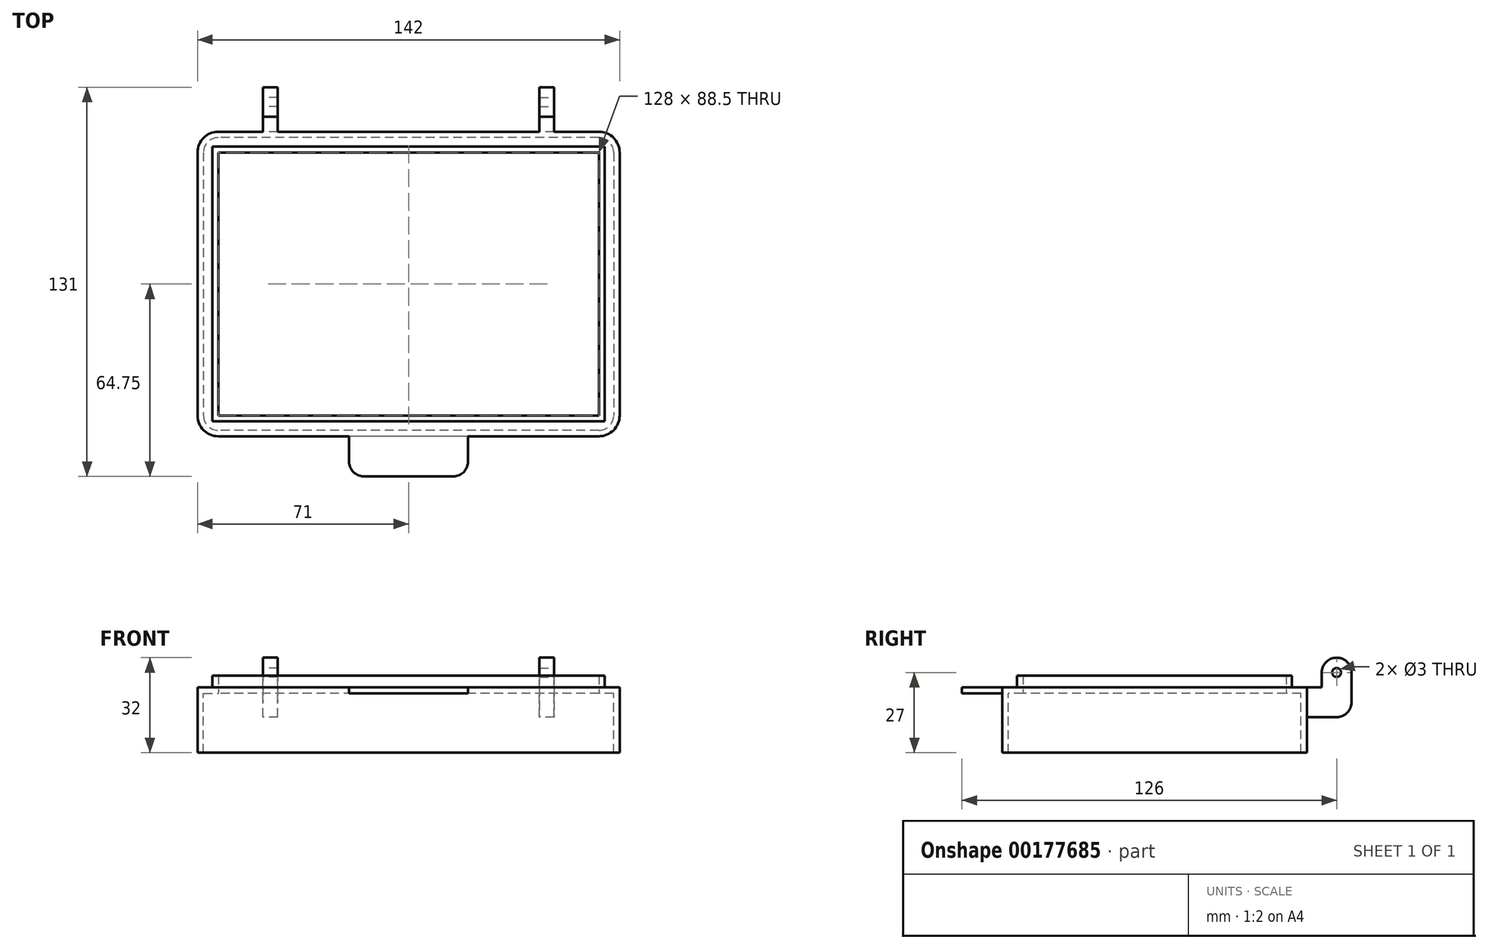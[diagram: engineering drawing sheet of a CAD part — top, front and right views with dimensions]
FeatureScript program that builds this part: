
annotation { "Feature Type Name" : "Feature", "Feature Type Description" : "" }
export const myFeature = defineFeature(function(context is Context, id is Id, definition is map)
    precondition{}
    {
        {
            var Q0;
            Q0=qCreatedBy(makeId("Top.planeOp"),FACE);
            var sketch = newSketch(context, id + "F0", { "sketchPlane" : qUnion([Q0])});
            skLineSegment(sketch, "E0.bottom", {"start": v(64, 49.25) * mm, "end": v(-64, 49.25) * mm});
            skLineSegment(sketch, "E0.top", {"start": v(64, -49.25) * mm, "end": v(-64, -49.25) * mm});
            skLineSegment(sketch, "E0.left", {"start": v(69, 44.25) * mm, "end": v(69, -44.25) * mm});
            skLineSegment(sketch, "E0.right", {"start": v(-69, 44.25) * mm, "end": v(-69, -44.25) * mm});
            skPoint(sketch, "E0.middle", {"position": v(0, 0) * mm});
            skPoint(sketch, "E1.visualSharp", {"position": v(-69, 49.25) * mm});
            skArc(sketch, "E1.filletArc", {"start": v(-64, 49.25) * mm, "mid": v(-67.54, 47.79) * mm, "end": v(-69, 44.25) * mm});
            skPoint(sketch, "E2.visualSharp", {"position": v(-69, -49.25) * mm});
            skArc(sketch, "E2.filletArc", {"start": v(-69, -44.25) * mm, "mid": v(-67.54, -47.79) * mm, "end": v(-64, -49.25) * mm});
            skPoint(sketch, "E3.visualSharp", {"position": v(69, -49.25) * mm});
            skArc(sketch, "E3.filletArc", {"start": v(64, -49.25) * mm, "mid": v(67.54, -47.79) * mm, "end": v(69, -44.25) * mm});
            skPoint(sketch, "E4.visualSharp", {"position": v(69, 49.25) * mm});
            skArc(sketch, "E4.filletArc", {"start": v(69, 44.25) * mm, "mid": v(67.54, 47.79) * mm, "end": v(64, 49.25) * mm});
            skArc(sketch, "E5.0", {"start": v(71, 44.25) * mm, "mid": v(68.95, 49.2) * mm, "end": v(64, 51.25) * mm});
            skLineSegment(sketch, "E5.1", {"start": v(71, 44.25) * mm, "end": v(71, -44.25) * mm});
            skLineSegment(sketch, "E5.2", {"start": v(64, 51.25) * mm, "end": v(-64, 51.25) * mm});
            skArc(sketch, "E5.3", {"start": v(64, -51.25) * mm, "mid": v(68.95, -49.2) * mm, "end": v(71, -44.25) * mm});
            skArc(sketch, "E5.4", {"start": v(-64, 51.25) * mm, "mid": v(-68.95, 49.2) * mm, "end": v(-71, 44.25) * mm});
            skLineSegment(sketch, "E5.5", {"start": v(-71, 44.25) * mm, "end": v(-71, -44.25) * mm});
            skArc(sketch, "E5.6", {"start": v(-71, -44.25) * mm, "mid": v(-68.95, -49.2) * mm, "end": v(-64, -51.25) * mm});
            skLineSegment(sketch, "E5.7", {"start": v(64, -51.25) * mm, "end": v(-64, -51.25) * mm});
            skLineSegment(sketch, "E6.0", {"start": v(66, 46.25) * mm, "end": v(-66, 46.25) * mm});
            skLineSegment(sketch, "E6.1", {"start": v(66, 46.25) * mm, "end": v(66, -46.25) * mm});
            skLineSegment(sketch, "E6.2", {"start": v(66, -46.25) * mm, "end": v(-66, -46.25) * mm});
            skLineSegment(sketch, "E6.3", {"start": v(-66, 46.25) * mm, "end": v(-66, -46.25) * mm});
            skLineSegment(sketch, "E7.bottom", {"start": v(-15, -64.75) * mm, "end": v(15, -64.75) * mm});
            skLineSegment(sketch, "E7.left", {"start": v(-20, -59.75) * mm, "end": v(-20, -51.25) * mm});
            skLineSegment(sketch, "E7.right", {"start": v(20, -59.75) * mm, "end": v(20, -51.25) * mm});
            skPoint(sketch, "E7.middle", {"position": v(0, -51.25) * mm});
            skPoint(sketch, "E8.visualSharp", {"position": v(-20, -64.75) * mm});
            skArc(sketch, "E8.filletArc", {"start": v(-20, -59.75) * mm, "mid": v(-18.54, -63.29) * mm, "end": v(-15, -64.75) * mm});
            skPoint(sketch, "E9.visualSharp", {"position": v(20, -64.75) * mm});
            skArc(sketch, "E9.filletArc", {"start": v(15, -64.75) * mm, "mid": v(18.54, -63.29) * mm, "end": v(20, -59.75) * mm});
            skLineSegment(sketch, "E10.0", {"start": v(64, 44.25) * mm, "end": v(-64, 44.25) * mm});
            skLineSegment(sketch, "E10.1", {"start": v(64, 44.25) * mm, "end": v(64, -44.25) * mm});
            skLineSegment(sketch, "E10.2", {"start": v(64, -44.25) * mm, "end": v(-64, -44.25) * mm});
            skLineSegment(sketch, "E10.3", {"start": v(-64, 44.25) * mm, "end": v(-64, -44.25) * mm});
            skSolve(sketch);
        }
        {
            var Q0;
            Q0=makeQuery(id+"F0.imprint","IMPRINT",FACE,{"disambiguationData":[TD([[makeQuery(id+"F0.imprint","IMPRINT",EDGE,{"derivedFrom":sQuery(id+"F0.wireOp",EDGE,"E0.bottom")}),-1.0]])]});
            extrude(context, id + "F1", {"entities" : qUnion([Q0]), "oppositeDirection" : true, "depth" : 20 * mm});
        }
        {
            var Q0;
            Q0=makeQuery(id+"F0.imprint","IMPRINT",FACE,{"disambiguationData":[TD([[makeQuery(id+"F0.imprint","IMPRINT",EDGE,{"derivedFrom":sQuery(id+"F0.wireOp",EDGE,"E7.bottom")}),1.0]])]});
            var Q1;
            Q1=makeQuery(id+"F0.imprint","IMPRINT",FACE,{"disambiguationData":[TD([[makeQuery(id+"F0.imprint","IMPRINT",EDGE,{"derivedFrom":sQuery(id+"F0.wireOp",EDGE,"E0.bottom")}),-1.0]])]});
            var Q2;
            Q2=makeQuery(id+"F0.imprint","IMPRINT",FACE,{"disambiguationData":[TD([[makeQuery(id+"F0.imprint","IMPRINT",EDGE,{"derivedFrom":sQuery(id+"F0.wireOp",EDGE,"E0.bottom")}),1.0]])]});
            extrude(context, id + "F2", {"entities" : qUnion([Q0, Q1, Q2]), "operationType" : NewBodyOperationType.ADD, "depth" : 2 * mm});
        }
        {
            var Q0;
            Q0=makeQuery(id+"F0.imprint","IMPRINT",FACE,{"disambiguationData":[TD([[makeQuery(id+"F0.imprint","IMPRINT",EDGE,{"derivedFrom":sQuery(id+"F0.wireOp",EDGE,"E6.0")}),1.0]])]});
            extrude(context, id + "F3", {"entities" : qUnion([Q0]), "operationType" : NewBodyOperationType.ADD, "depth" : 6 * mm});
        }
        {
            var Q0;
            {var subQ0=sQuery(id+"F0.wireOp",EDGE,"E5.2");Q0=makeQuery(id+"F2.boolean.opBoolean","MERGE",FACE,{"derivedFrom":[makeQuery(id+"F1.opExtrude","SWEPT_FACE",FACE,{"disambiguationData":[OSD([subQ0])]}),makeQuery(id+"F2.opExtrude","SWEPT_FACE",FACE,{"disambiguationData":[OSD([subQ0])]})]});}
            var sketch = newSketch(context, id + "F4", { "sketchPlane" : qUnion([Q0])});
            skLineSegment(sketch, "E11.MirrorCS", {"start": v(-44, 2) * mm, "end": v(-44, -8) * mm});
            skLineSegment(sketch, "E12.MirrorCS", {"start": v(-49, -8) * mm, "end": v(-44, -8) * mm});
            skLineSegment(sketch, "E13.MirrorCS", {"start": v(-49, 2) * mm, "end": v(-49, -8) * mm});
            skSolve(sketch);
        }
        {
            var Q0;
            Q0 = qSketchRegion(id + "F4", true);
            var Q1;
            {var subQ0=sQuery(id+"F4.wireOp",EDGE,"E11.MirrorCS");Q1=makeQuery(id+"F4.imprint","IMPRINT",FACE,{"disambiguationData":[TD([[makeQuery(id+"F4.imprint","IMPRINT",EDGE,{"derivedFrom":subQ0}),-1.0]])]});}
            extrude(context, id + "F5", {"entities" : qUnion([Q0, Q1]), "operationType" : NewBodyOperationType.ADD, "depth" : 10 * mm});
        }
        {
            var Q0;
            Q0=makeQuery(id+"F5.opExtrude","SWEPT_FACE",FACE,{"disambiguationData":[OSD([sQuery(id+"F4.wireOp",EDGE,"E13.MirrorCS")])]});
            var sketch = newSketch(context, id + "F6", { "sketchPlane" : qUnion([Q0])});
            skLineSegment(sketch, "E14.bottom", {"start": v(61.25, -8) * mm, "end": v(61.25, -8) * mm});
            skLineSegment(sketch, "E14.top", {"start": v(61.25, 12) * mm, "end": v(61.25, 12) * mm});
            skLineSegment(sketch, "E14.left", {"start": v(61.25, -8) * mm, "end": v(61.25, 12) * mm});
            skLineSegment(sketch, "E14.right", {"start": v(66.25, -3) * mm, "end": v(66.25, 7) * mm});
            skLineSegment(sketch, "E15.top", {"start": v(61.25, 2) * mm, "end": v(56.25, 2) * mm});
            skLineSegment(sketch, "E15.left", {"start": v(61.25, 12) * mm, "end": v(61.25, 2) * mm});
            skLineSegment(sketch, "E15.right", {"start": v(56.25, 7) * mm, "end": v(56.25, 2) * mm});
            skPoint(sketch, "E16", {"position": v(61.25, 7) * mm});
            skCircle(sketch, "E17", {"center": v(61.25, 7) * mm, "radius": 1.5 * mm});
            skPoint(sketch, "E18.visualSharp", {"position": v(56.25, 12) * mm});
            skArc(sketch, "E18.filletArc", {"start": v(61.25, 12) * mm, "mid": v(57.71, 10.54) * mm, "end": v(56.25, 7) * mm});
            skPoint(sketch, "E19.visualSharp", {"position": v(66.25, 12) * mm});
            skArc(sketch, "E19.filletArc", {"start": v(66.25, 7) * mm, "mid": v(64.79, 10.54) * mm, "end": v(61.25, 12) * mm});
            skPoint(sketch, "E20.visualSharp", {"position": v(66.25, -8) * mm});
            skArc(sketch, "E20.filletArc", {"start": v(61.25, -8) * mm, "mid": v(64.79, -6.54) * mm, "end": v(66.25, -3) * mm});
            skSolve(sketch);
        }
        {
            var Q0;
            Q0 = qSketchRegion(id + "F6", true);
            extrude(context, id + "F7", {"entities" : qUnion([Q0]), "operationType" : NewBodyOperationType.ADD, "oppositeDirection" : true, "depth" : 5 * mm});
        }
        {
            var Q0;
            Q0=qCreatedBy(makeId("Right.planeOp"),FACE);
            cPlane(context, id + "F8", {"entities" : qUnion([Q0]), "cplaneType" : CPlaneType.OFFSET, "offset" : 49 * mm, "oppositeDirection" : true, "width" : 150 * mm, "height" : 150 * mm});
        }
        {
            var Q0;
            Q0=qCreatedBy(id+"F8.planeOp",FACE);
            var sketch = newSketch(context, id + "F9", { "sketchPlane" : qUnion([Q0])});
            skLineSegment(sketch, "E21.0.0", {"start": v(51.25, 2) * mm, "end": v(56.25, 2) * mm});
            skLineSegment(sketch, "E21.0.1", {"start": v(56.25, 2) * mm, "end": v(56.25, 7) * mm});
            skArc(sketch, "E21.0.2", {"start": v(56.25, 7) * mm, "mid": v(61.25, 12) * mm, "end": v(66.25, 7) * mm});
            skLineSegment(sketch, "E21.0.3", {"start": v(66.25, 7) * mm, "end": v(66.25, -3) * mm});
            skArc(sketch, "E21.0.4", {"start": v(66.25, -3) * mm, "mid": v(64.79, -6.54) * mm, "end": v(61.25, -8) * mm});
            skLineSegment(sketch, "E21.0.5", {"start": v(61.25, -8) * mm, "end": v(51.25, -8) * mm});
            skLineSegment(sketch, "E21.0.6", {"start": v(51.25, -8) * mm, "end": v(51.25, 2) * mm});
            skCircle(sketch, "E22.0", {"center": v(61.25, 7) * mm, "radius": 1.5 * mm});
            skSolve(sketch);
        }
        {
            var Q0;
            Q0 = qSketchRegion(id + "F9", true);
            extrude(context, id + "F10", {"entities" : qUnion([Q0]), "operationType" : NewBodyOperationType.ADD, "depth" : 5 * mm});
        }
    });
